FREECAD ASSEMBLY — COMPONENT RECIPES ("composit_stand11")

This assembly document has 29 components, labeled P0..P28 below (a component is one placed body or linked part). 28 of them carry a construction recipe — the FreeCAD feature program that regenerates the part from scratch, quoted from this document or its linked companion documents; the rest are supplied as boundary geometry only. No exploded tour is included for this assembly.
NOTE — document 2 of 2 of this assembly tour. The two overview renders and the header above are repeated from document 1; the component sections below continue where the previous document stopped.
COMPONENT P27 — recipe-attached ("module_Body", modeled in this document).
Construction recipe (the document's own serialized feature program — sketch geometry with constraints, then the solid features built on it; lengths are millimeters unless a unit is written):

FEATURE [PartDesign::SubShapeBinder] Binder
  BindCopyOnChange = 0
  BindMode = 0
  ClaimChildren = true
  Context = -> Body [Binder.]
  Fuse = false
  MakeFace = true
  OffsetFill = false
  OffsetIntersection = false
  OffsetJoinType = 0
  OffsetOpenResult = false
  PartialLoad = false
  Relative = false
  Support = -> [Connect]
  _Version = 2
FEATURE [PartDesign::FeaturePython] BaseBend  # WARN: FeaturePython — macro-defined, semantics opaque (R4)
  BendSide = 1
  BendSketch = -> Binder
  MidPlane = false
  Reverse = false
  Suppressed = false
  length = 1100
  radius = 0.1
  thickness = 0.3
  expr: length = <<Properties>>.modules_fix_height
FEATURE [PartDesign::CoordinateSystem] Local_CS005  label="face_base_placement"
  AttacherType = Attacher::AttachEngine3D
  AttachmentSupport = -> [XY_Plane]
  MapMode = 5
FEATURE [PartDesign::FeaturePython] Extend  # WARN: FeaturePython — macro-defined, semantics opaque (R4)
  BaseFeature = -> BaseBend
  Offset = 0.02
  Refine = true
  Suppressed = false
  UseSubtraction = false
  baseObject = -> BaseBend [Face1]
  gap1 = 0
  gap2 = 0
  length = 0
FEATURE [PartDesign::FeaturePython] Bend  # WARN: FeaturePython — macro-defined, semantics opaque (R4)
  AutoMiter = false
  BaseFeature = -> Extend
  BendType = 0
  LengthList = [0.1]
  LengthSpec = 0
  ReliefFactor = 0.7
  Suppressed = false
  UseReliefFactor = false
  angle = 90
  baseObject = -> Extend [Edge119,Edge104,Edge124,Edge75,Edge58,Edge122,Edge29,Edge14]
  bendAList = [90]
  extend1 = 0
  extend2 = 0
  gap1 = 0
  gap2 = 0
  invert = true
  kfactor = 0.5
  length = 0.1
  maxExtendDist = 5
  minGap = 0.2
  minReliefGap = 1
  miterangle1 = 0
  miterangle2 = 0
  offset = 0
  radius = 0.1
  reliefType = 0
  reliefd = 1
  reliefw = 0.8
  sketchflip = false
  sketchinvert = false
  unfold = false
  expr: radius = BaseBend.radius
FEATURE [PartDesign::CoordinateSystem] Local_CS009  label="face_section_LCS"
  AttacherType = Attacher::AttachEngine3D
  AttachmentOffset = pos=(319.563,20,0) rot=(0,0,1;0rad)
  AttachmentSupport = -> [XY_Plane]
  MapMode = 5
  Placement = pos=(319.563,20,0) rot=(0,0,1;0rad)
  expr: .AttachmentOffset.Base.x = <<mid_Sketch>>.Constraints.middle
  expr: .AttachmentOffset.Base.y = <<base_Sketch>>.Constraints.offset
FEATURE [PartDesign::CoordinateSystem] Local_CS006  label="sink1_placement"
  AttacherType = Attacher::AttachEngine3D
  AttachmentOffset = pos=(0,0,100) rot=(0,0,1;0rad)
  AttachmentSupport = -> [Local_CS009]
  MapMode = 5
  Placement = pos=(319.563,20,100) rot=(0,0,1;0rad)
  expr: .AttachmentOffset.Base.z = <<sink_placement>>.Placement.Base.z
FEATURE [PartDesign::CoordinateSystem] Local_CS007  label="sink2_placement"
  AttacherType = Attacher::AttachEngine3D
  AttachmentOffset = pos=(-639.126,0,0) rot=(0,0,1;0rad)
  AttachmentSupport = -> [Local_CS006]
  MapMode = 5
  Placement = pos=(-319.563,20,100) rot=(0,0,1;0rad)
  expr: .AttachmentOffset.Base.x = -<<mid_Sketch>>.Constraints.middle * 2
FEATURE [PartDesign::CoordinateSystem] Local_CS010  label="dropper_comp_fix1"
  AttacherType = Attacher::AttachEngine3D
  AttachmentOffset = pos=(0,0,1100) rot=(0,0,1;0rad)
  AttachmentSupport = -> [Local_CS009]
  MapMode = 5
  Placement = pos=(319.563,20,1100) rot=(0,0,1;0rad)
  expr: .AttachmentOffset.Base.z = <<Properties>>.modules_fix_height
FEATURE [PartDesign::CoordinateSystem] Local_CS011  label="dropper_comp_fix2"
  AttacherType = Attacher::AttachEngine3D
  AttachmentOffset = pos=(-639.126,0,0) rot=(0,0,1;0rad)
  AttachmentSupport = -> [Local_CS010]
  MapMode = 5
  Placement = pos=(-319.563,20,1100) rot=(0,0,1;0rad)
  expr: .AttachmentOffset.Base.x = -<<mid_Sketch>>.Constraints.middle * 2
FEATURE [PartDesign::CoordinateSystem] Local_CS014  label="bar1_placement"
  AttacherType = Attacher::AttachEngine3D
  AttachmentSupport = -> [LinearArray004]
  MapMode = 1
  Placement = pos=(-636.126,17,220) rot=(0.707107,0,0.707107;3.14159rad)
FEATURE [PartDesign::CoordinateSystem] Local_CS015  label="bar2_placement"
  AttacherType = Attacher::AttachEngine3D
  AttachmentSupport = -> [LinearArray004]
  MapMode = 1
  Placement = pos=(-636.126,17,883.5) rot=(0.707107,0,0.707107;3.14159rad)
FEATURE [PartDesign::CoordinateSystem] Local_CS024
  AttacherType = Attacher::AttachEngine3D
  AttachmentOffset = pos=(319.563,0,0) rot=(0,1,0;3.14159rad)
  AttachmentSupport = -> [XY_Plane]
  MapMode = 5
  Placement = pos=(319.563,0,0) rot=(0,1,0;3.14159rad)
  expr: .AttachmentOffset.Base.x = <<mid_Sketch>>.Constraints.middle
FEATURE [PartDesign::CoordinateSystem] Local_CS025  label="face_lamp_fix_LCS"
  AttacherType = Attacher::AttachEngine3D
  AttachmentOffset = pos=(319.563,0,182) rot=(0,0,1;0rad)
  AttachmentSupport = -> [XY_Plane]
  MapMode = 5
  Placement = pos=(319.563,0,182) rot=(0,0,1;0rad)
  expr: AttachmentOffset = <<face_lamp_fix_placement>>.Placement
FEATURE [Sketcher::SketchObject] Sketch075
  AttachmentOffset = pos=(0,0,0) rot=(0,0.707107,0.707107;3.14159rad)
  FullyConstrained = true
  MapMode = 5
  Placement = pos=(484.198,20,100) rot=(0,0.707107,0.707107;3.14159rad)
  sketch-geometry (5):
    g0: LineSegment StartX=18.7482 StartY=0 StartZ=0 EndX=-1 EndY=0 EndZ=0
    g1: LineSegment StartX=-1 StartY=0 StartZ=0 EndX=-1 EndY=15 EndZ=0
    g2: LineSegment StartX=-1 StartY=15 StartZ=0 EndX=1 EndY=15 EndZ=0
    g3: ArcOfCircle CenterX=1 CenterY=0 CenterZ=0 NormalX=0 NormalY=0 NormalZ=1 AngleXU=0 Radius=15 StartAngle=0.167448 EndAngle=1.5708
    g4: ArcOfCircle CenterX=18.7482 CenterY=3 CenterZ=0 NormalX=0 NormalY=0 NormalZ=1 AngleXU=0 Radius=3 StartAngle=3.30904 EndAngle=4.71239
  constraints (14):
    c: PointOnObject(g0,g-1)
    c: Horizontal(g0)
    c: Coincident(g0,g1)
    c: Vertical(g1)
    c: Coincident(g1,g2)
    c: Horizontal(g2)
    c: PointOnObject(g3,g-1)
    c: Tangent(g4,g0) = 1.5708
    c: Tangent(g3,g2) = 1.5708
    c: Tangent(g4,g3) = 1.5708
    c: Radius(g4) = 3
    c: Radius(g3) = 15
    c: DistanceX(g2) = 1
    c: DistanceX(g1) = -1
FEATURE [Sketcher::SketchObject] Sketch076
  AttachmentOffset = pos=(0,0,0) rot=(0.889126,0.323616,0.323616;1.68804rad)
  FullyConstrained = true
  MapMode = 5
  Placement = pos=(484.198,20,100) rot=(0.889126,0.323616,0.323616;1.68804rad)
  expr: .AttachmentOffset.Rotation.Yaw = <<base_Sketch>>.Constraints.angle
  sketch-geometry (5):
    g0: LineSegment StartX=18.7482 StartY=0 StartZ=0 EndX=-1 EndY=0 EndZ=0
    g1: LineSegment StartX=-1 StartY=0 StartZ=0 EndX=-1 EndY=15 EndZ=0
    g2: LineSegment StartX=-1 StartY=15 StartZ=0 EndX=1 EndY=15 EndZ=0
    g3: ArcOfCircle CenterX=1 CenterY=0 CenterZ=0 NormalX=0 NormalY=0 NormalZ=1 AngleXU=0 Radius=15 StartAngle=0.167448 EndAngle=1.5708
    g4: ArcOfCircle CenterX=18.7482 CenterY=3 CenterZ=0 NormalX=0 NormalY=0 NormalZ=1 AngleXU=0 Radius=3 StartAngle=3.30904 EndAngle=4.71239
  constraints (14):
    c: PointOnObject(g0,g-1)
    c: PointOnObject(g0,g-1)
    c: Coincident(g0,g1)
    c: Vertical(g1)
    c: Coincident(g1,g2)
    c: Horizontal(g2)
    c: PointOnObject(g3,g-1)
    c: Tangent(g3,g2) = 1.5708
    c: Tangent(g4,g0) = 1.5708
    c: Tangent(g4,g3) = 1.5708
    c: DistanceX(g2) = 1
    c: DistanceY(g1,g1) = 15
    c: DistanceX(g1) = -1
    c: Radius(g4) = 3
FEATURE [PartDesign::Plane] DatumPlane004
  Length = 65.8114
  MapMode = 4
  Placement = pos=(319.563,20,100) rot=(0.57735,0.57735,0.57735;2.0944rad)
  ResizeMode = 0
  Width = 140.811
FEATURE [PartDesign::Plane] DatumPlane005
  Length = 60
  MapMode = 4
  Placement = pos=(0,0,0) rot=(0.57735,0.57735,0.57735;2.0944rad)
  ResizeMode = 0
  Width = 60
FEATURE [PartDesign::Mirrored] Mirrored008
  MirrorPlane = -> DatumPlane004
  Suppressed = false
FEATURE [PartDesign::LinearPattern] LinearPattern004
  Direction = -> Sketch075 [H_Axis]
  Length = 639.126
  Mode = 0
  Occurrences = 2
  Offset = 639.126
  Suppressed = false
  expr: Length = <<Dimensions>>.Constraints.modules_middle_distance * 2
FEATURE [PartDesign::CoordinateSystem] Local_CS032  label="face_top_LCS"
  AttacherType = Attacher::AttachEngine3D
  AttachmentOffset = pos=(0,0,1100) rot=(0,0,1;0rad)
  MapMode = 5
  Placement = pos=(0,0,1100) rot=(0,0,1;0rad)
  expr: .AttachmentOffset.Base.z = <<Properties>>.modules_fix_height
FEATURE [PartDesign::CoordinateSystem] Local_CS034
  AttacherType = Attacher::AttachEngine3D
  AttachmentOffset = pos=(-639.126,60,480) rot=(0.57735,-0.57735,-0.57735;2.0944rad)
  MapMode = 5
  Placement = pos=(-639.126,60,480) rot=(0.57735,-0.57735,-0.57735;2.0944rad)
  expr: AttachmentOffset = <<shield_placement>>.Placement
FEATURE [PartDesign::Boolean] Boolean
  BaseFeature = -> Bend
  Group = -> [Compound001]
  Refine = true
  Suppressed = false
  Type = 1
  UsePlacement = false
FEATURE [PartDesign::Boolean] Boolean013
  BaseFeature = -> Boolean
  Group = -> [Compound007]
  Suppressed = false
  Type = 1
  UsePlacement = true
FEATURE [PartDesign::Boolean] Boolean014
  BaseFeature = -> Boolean013
  Group = -> [Compound005]
  Refine = true
  Suppressed = false
  Type = 0
  UsePlacement = true
FEATURE [PartDesign::Pocket] Pocket022
  BaseFeature = -> Boolean014
  Direction = (0,-1,2e-16)
  Length = 5
  Length2 = 0.1
  Profile = -> Sketch075
  ReferenceAxis = -> Sketch075 [N_Axis]
  Suppressed = false
  Type = 4
FEATURE [PartDesign::Pocket] Pocket023
  BaseFeature = -> Pocket022
  Direction = (-0.642788,0.766044,0)
  Length = 0.1
  Length2 = 5
  Midplane = true
  Profile = -> Sketch076
  ReferenceAxis = -> Sketch076 [N_Axis]
  Suppressed = false
  Type = 4
FEATURE [PartDesign::MultiTransform] MultiTransform004
  BaseFeature = -> Pocket023
  Originals = -> [Pocket022,Pocket023]
  Suppressed = false
  Transformations = -> [Mirrored008,LinearPattern004]
FEATURE [PartDesign::Body] Body  label="face"
  Group = -> [Binder,BaseBend,Extend,Bend,Boolean,Boolean013,Local_CS009,Local_CS005,Local_CS006,Local_CS007,Local_CS010,Local_CS011,Local_CS014,Local_CS015,Local_CS024,Local_CS025,Boolean014,Sketch075,Sketch076,Pocket022,Pocket023,DatumPlane004,DatumPlane005,MultiTransform004,Mirrored008,LinearPattern004,Local_CS032,Local_CS034]
  Origin = -> Origin
  Tip = -> MultiTransform004
COMPONENT P28 — geometry summary ("modules"; no construction recipe available for this part):
  bounding box: 1220.6 x 970.0 x 137.1 mm
  tessellated surface: 360,096 triangles
  volume: 16054997257454379676075496254509199119899785434639068064063372245540747675981731400751099634202854817792 mm^3 (9887628150821226908688576681887324159217648573793799610549357154315061577400876020368347456602112% of its bounding box)
  symmetry: mirror-symmetric across its x mid-plane
PROVENANCE & LICENSES
A FreeCAD (.FCStd) document from a public repository crawl; recipes are the document's own serialized feature recipes (and, for linked parts, companion documents' recipes).
License: as declared in the source repository (recorded in the dataset sidecar).
